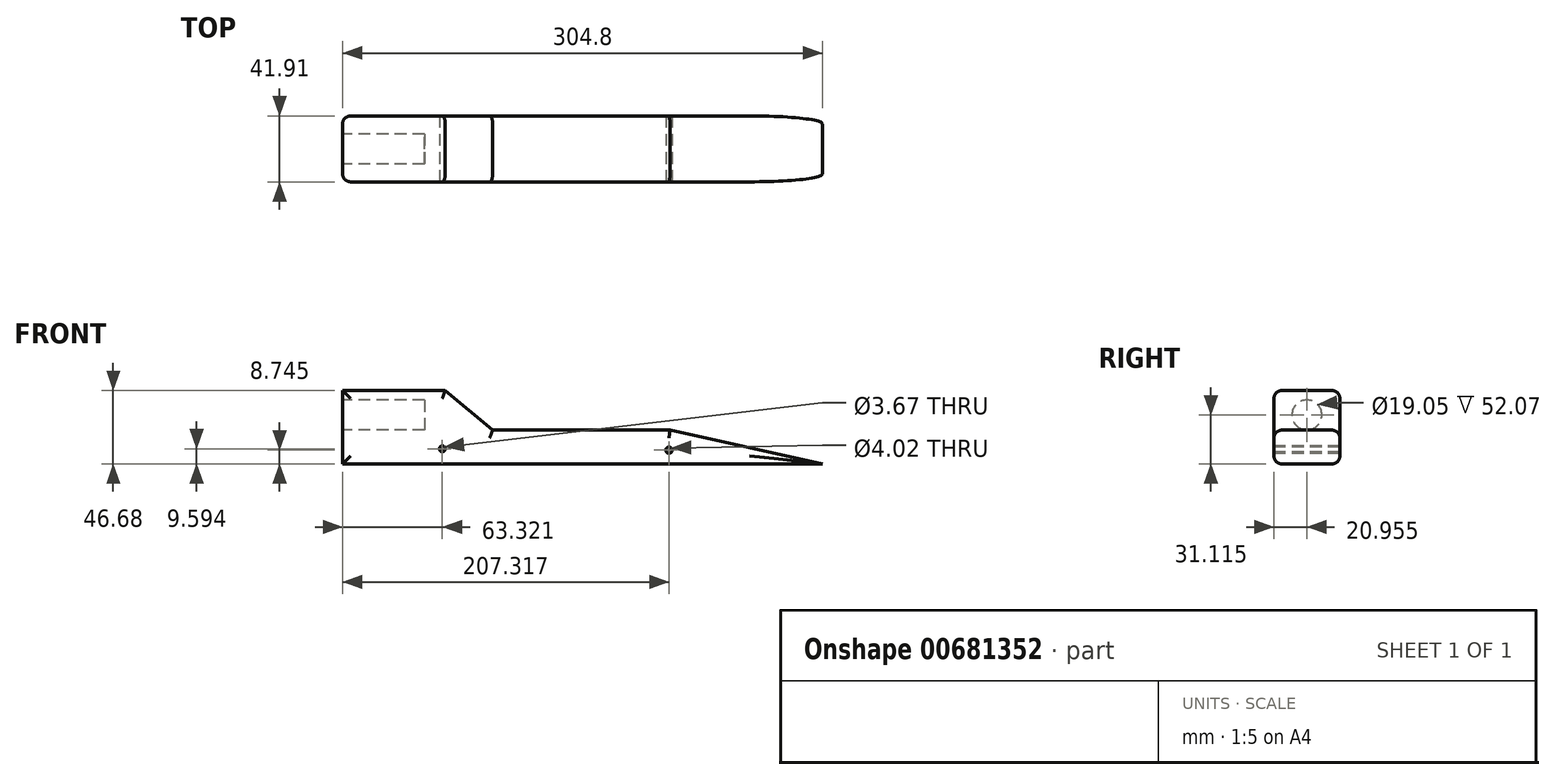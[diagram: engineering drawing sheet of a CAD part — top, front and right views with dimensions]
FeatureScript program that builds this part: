
annotation { "Feature Type Name" : "Feature", "Feature Type Description" : "" }
export const myFeature = defineFeature(function(context is Context, id is Id, definition is map)
    precondition{}
    {
        {
            var Q0;
            Q0=qCreatedBy(makeId("Top.planeOp"),FACE);
            var sketch = newSketch(context, id + "F0", { "sketchPlane" : qUnion([Q0])});
            skLineSegment(sketch, "E0.bottom", {"start": v(0, 0) * mm, "end": v(304.8, 0) * mm});
            skLineSegment(sketch, "E0.top", {"start": v(0, 41.91) * mm, "end": v(304.8, 41.91) * mm});
            skLineSegment(sketch, "E0.left", {"start": v(0, 0) * mm, "end": v(0, 41.91) * mm});
            skLineSegment(sketch, "E0.right", {"start": v(304.8, 0) * mm, "end": v(304.8, 41.91) * mm});
            skSolve(sketch);
        }
        {
            var Q0;
            Q0=makeQuery(id+"F0.imprint","IMPRINT",FACE,{"disambiguationData":[TD([[makeQuery(id+"F0.imprint","IMPRINT",EDGE,{"derivedFrom":sQuery(id+"F0.wireOp",EDGE,"E0.bottom")}),1.0]])]});
            extrude(context, id + "F1", {"entities" : qUnion([Q0]), "depth" : 72.39 * mm, "offsetDistance" : 25.4 * mm});
        }
        {
            var Q0;
            Q0=makeQuery(id+"F1.opExtrude","SWEPT_FACE",FACE,{"disambiguationData":[OSD([sQuery(id+"F0.wireOp",EDGE,"E0.bottom")])]});
            var sketch = newSketch(context, id + "F2", { "sketchPlane" : qUnion([Q0])});
            skLineSegment(sketch, "E1", {"start": v(0, 72.4) * mm, "end": v(304.8, 19.05) * mm});
            skLineSegment(sketch, "E2", {"start": v(304.8, 19.05) * mm, "end": v(304.8, 0) * mm});
            skSolve(sketch);
        }
        {
            var Q0;
            Q0=qSketchRegion(id+"F2",true);
            var Q1;
            {var subQ0=sQuery(id+"F2.wireOp",EDGE,"E1");Q1=makeQuery(id+"F2.imprint","IMPRINT",FACE,{"disambiguationData":[TD([[makeQuery(id+"F2.imprint","IMPRINT",EDGE,{"derivedFrom":subQ0}),1.0]])]});}
            extrude(context, id + "F3", {"entities" : qUnion([Q0, Q1]), "operationType" : NewBodyOperationType.REMOVE, "oppositeDirection" : true, "depth" : 44.45 * mm, "offsetDistance" : 25.4 * mm});
        }
        {
            var Q0;
            Q0=makeQuery(id+"F1.opExtrude","SWEPT_FACE",FACE,{"disambiguationData":[OSD([sQuery(id+"F0.wireOp",EDGE,"E0.left")])]});
            var sketch = newSketch(context, id + "F4", { "sketchPlane" : qUnion([Q0])});
            skCircle(sketch, "E3", {"center": v(-20.96, 31.12) * mm, "radius": 9.53 * mm});
            skSolve(sketch);
        }
        {
            var Q0;
            Q0=makeQuery(id+"F4.imprint","IMPRINT",FACE,{"disambiguationData":[TD([[makeQuery(id+"F4.imprint","IMPRINT",EDGE,{"derivedFrom":sQuery(id+"F4.wireOp",EDGE,"E3")}),1.0]])]});
            extrude(context, id + "F5", {"entities" : qUnion([Q0]), "operationType" : NewBodyOperationType.REMOVE, "oppositeDirection" : true, "depth" : 52.07 * mm, "offsetDistance" : 25.4 * mm});
        }
        {
            var Q0;
            Q0=makeQuery(id+"F1.opExtrude","SWEPT_FACE",FACE,{"disambiguationData":[OSD([sQuery(id+"F0.wireOp",EDGE,"E0.bottom")])]});
            var sketch = newSketch(context, id + "F6", { "sketchPlane" : qUnion([Q0])});
            skLineSegment(sketch, "E4", {"start": v(0, 53.75) * mm, "end": v(68.94, 53.75) * mm});
            skLineSegment(sketch, "E5", {"start": v(68.94, 53.75) * mm, "end": v(95.29, 29.8) * mm});
            skLineSegment(sketch, "E6", {"start": v(95.29, 29.8) * mm, "end": v(207.87, 29.8) * mm});
            skLineSegment(sketch, "E7", {"start": v(207.87, 29.8) * mm, "end": v(304.8, 0) * mm});
            skLineSegment(sketch, "E8", {"start": v(304.8, 0) * mm, "end": v(0, 0) * mm});
            skLineSegment(sketch, "E9", {"start": v(0, 0) * mm, "end": v(0, 53.75) * mm});
            skSolve(sketch);
        }
        {
            var Q0;
            {var subQ0=sQuery(id+"F6.wireOp",EDGE,"E4");Q0=makeQuery(id+"F6.imprint","IMPRINT",FACE,{"disambiguationData":[TD([[makeQuery(id+"F6.imprint","IMPRINT",EDGE,{"derivedFrom":subQ0}),1.0]])]});}
            extrude(context, id + "F7", {"entities" : qUnion([Q0]), "operationType" : NewBodyOperationType.REMOVE, "oppositeDirection" : true, "depth" : 42.16 * mm, "offsetDistance" : 25.4 * mm});
        }
        {
            var Q0;
            Q0=makeQuery(id+"F1.opExtrude","SWEPT_FACE",FACE,{"disambiguationData":[OSD([sQuery(id+"F0.wireOp",EDGE,"E0.bottom")])]});
            var sketch = newSketch(context, id + "F8", { "sketchPlane" : qUnion([Q0])});
            skLineSegment(sketch, "E10", {"start": v(0, 46.68) * mm, "end": v(65.16, 46.68) * mm});
            skLineSegment(sketch, "E11", {"start": v(65.16, 46.68) * mm, "end": v(95.29, 21.53) * mm});
            skLineSegment(sketch, "E12", {"start": v(95.29, 21.53) * mm, "end": v(207.87, 21.53) * mm});
            skLineSegment(sketch, "E13", {"start": v(207.87, 21.53) * mm, "end": v(304.8, 0) * mm});
            skLineSegment(sketch, "E14", {"start": v(304.8, 0) * mm, "end": v(0, 0) * mm});
            skLineSegment(sketch, "E15", {"start": v(0, 0) * mm, "end": v(0, 46.68) * mm});
            skSolve(sketch);
        }
        {
            var Q0;
            {var subQ0=sQuery(id+"F8.wireOp",EDGE,"E10");Q0=makeQuery(id+"F8.imprint","IMPRINT",FACE,{"disambiguationData":[TD([[makeQuery(id+"F8.imprint","IMPRINT",EDGE,{"derivedFrom":subQ0}),1.0]])]});}
            extrude(context, id + "F9", {"entities" : qUnion([Q0]), "operationType" : NewBodyOperationType.REMOVE, "oppositeDirection" : true, "depth" : 43.18 * mm, "offsetDistance" : 25.4 * mm});
        }
        {
            var Q0;
            Q0=makeQuery(id+"F1.opExtrude","SWEPT_FACE",FACE,{"disambiguationData":[OSD([sQuery(id+"F0.wireOp",EDGE,"E0.bottom")])]});
            fillet(context, id + "F10", {"entities" : qUnion([Q0]), "radius" : 5.08 * mm, "tangentPropagation" : true, "allowEdgeOverflow" : false});
        }
        {
            var Q0;
            Q0=makeQuery(id+"F1.opExtrude","SWEPT_FACE",FACE,{"disambiguationData":[OSD([sQuery(id+"F0.wireOp",EDGE,"E0.top")])]});
            fillet(context, id + "F11", {"entities" : qUnion([Q0]), "radius" : 5.08 * mm, "tangentPropagation" : true, "allowEdgeOverflow" : false});
        }
        {
            var Q0;
            Q0=makeQuery(id+"F1.opExtrude","SWEPT_FACE",FACE,{"disambiguationData":[OSD([sQuery(id+"F0.wireOp",EDGE,"E0.bottom")])]});
            var sketch = newSketch(context, id + "F12", { "sketchPlane" : qUnion([Q0])});
            skCircle(sketch, "E16", {"center": v(63.32, 9.6) * mm, "radius": 1.84 * mm});
            skCircle(sketch, "E17", {"center": v(207.32, 9.6) * mm, "radius": 1.67 * mm});
            skSolve(sketch);
        }
        {
            var Q0;
            Q0=makeQuery(id+"F12.imprint","IMPRINT",FACE,{"disambiguationData":[TD([[makeQuery(id+"F12.imprint","IMPRINT",EDGE,{"derivedFrom":sQuery(id+"F12.wireOp",EDGE,"E16")}),1.0]])]});
            extrude(context, id + "F13", {"entities" : qUnion([Q0]), "operationType" : NewBodyOperationType.REMOVE, "oppositeDirection" : true, "depth" : 50.8 * mm, "offsetDistance" : 25.4 * mm});
        }
        {
            var Q0;
            Q0=makeQuery(id+"F1.opExtrude","SWEPT_FACE",FACE,{"disambiguationData":[OSD([sQuery(id+"F0.wireOp",EDGE,"E0.bottom")])]});
            var sketch = newSketch(context, id + "F14", { "sketchPlane" : qUnion([Q0])});
            skCircle(sketch, "E18", {"center": v(207.32, 8.75) * mm, "radius": 2 * mm});
            skSolve(sketch);
        }
        {
            var Q0;
            Q0 = qSketchRegion(id + "F14", true);
            extrude(context, id + "F15", {"entities" : qUnion([Q0]), "operationType" : NewBodyOperationType.REMOVE, "oppositeDirection" : true, "depth" : 50.8 * mm, "offsetDistance" : 25.4 * mm});
        }
    });
